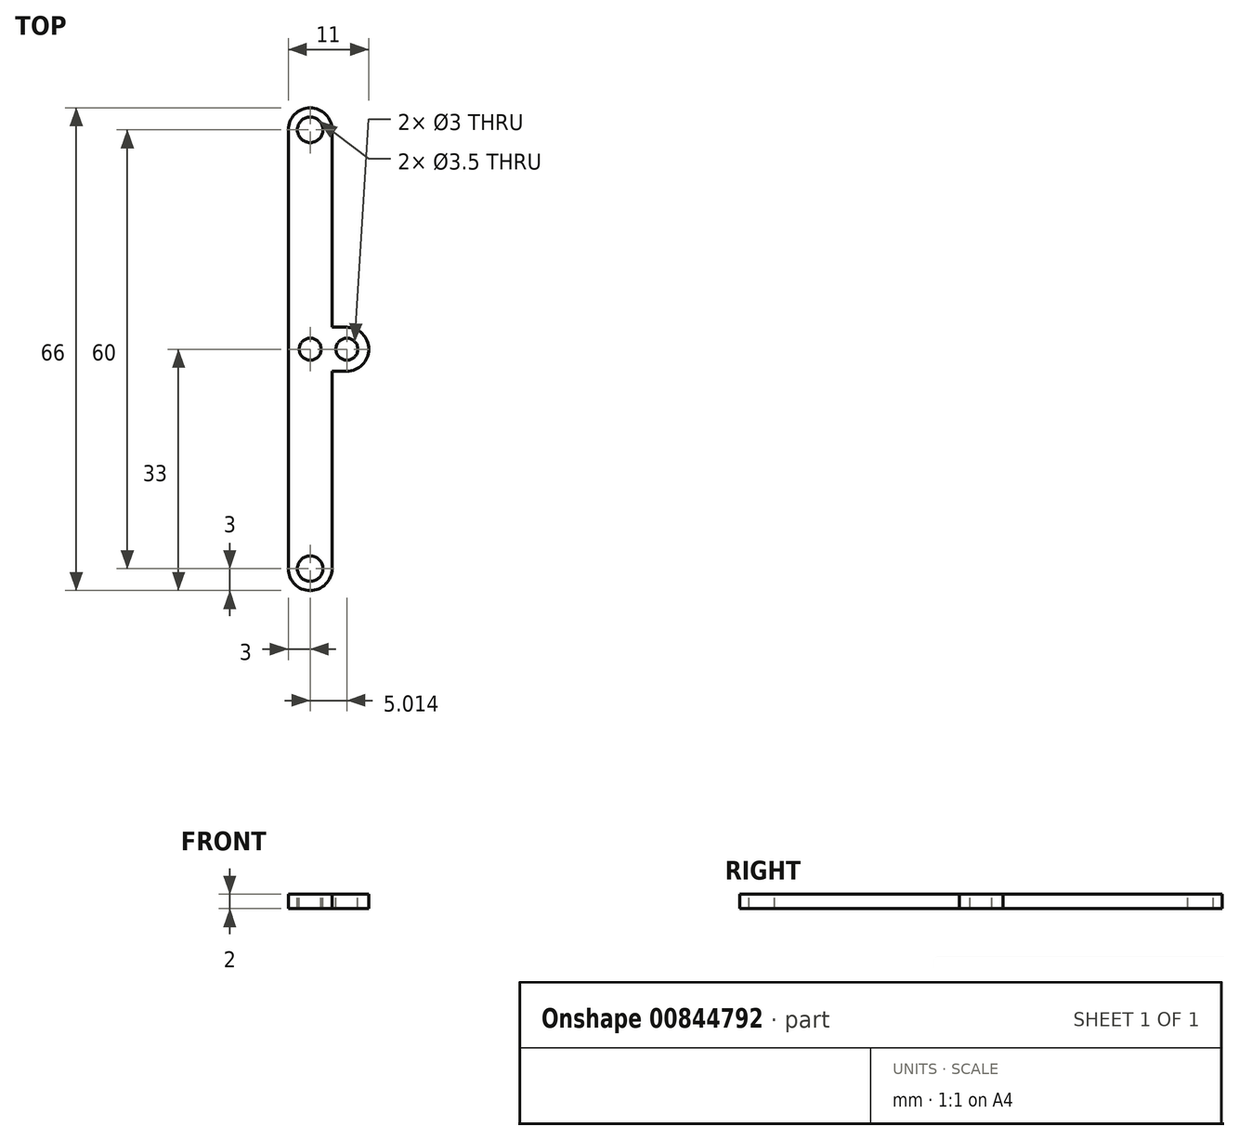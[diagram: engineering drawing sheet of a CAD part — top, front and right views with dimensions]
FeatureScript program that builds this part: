
annotation { "Feature Type Name" : "Feature", "Feature Type Description" : "" }
export const myFeature = defineFeature(function(context is Context, id is Id, definition is map)
    precondition{}
    {
        {
            var Q0;
            Q0=qCreatedBy(makeId("Top.planeOp"),FACE);
            var sketch = newSketch(context, id + "F0", { "sketchPlane" : qUnion([Q0])});
            skLineSegment(sketch, "E0.bottom", {"start": v(-3, 33) * mm, "end": v(3, 33) * mm});
            skLineSegment(sketch, "E0.top", {"start": v(-3, -33) * mm, "end": v(3, -33) * mm});
            skLineSegment(sketch, "E0.left", {"start": v(-3, 33) * mm, "end": v(-3, -33) * mm});
            skLineSegment(sketch, "E0.right", {"start": v(3, 33) * mm, "end": v(3, -33) * mm});
            skPoint(sketch, "E0.middle", {"position": v(0, 0) * mm});
            skSolve(sketch);
        }
        {
            var Q0;
            Q0=qSketchRegion(id+"F0",true);
            extrude(context, id + "F1", {"entities" : qUnion([Q0]), "depth" : 2 * mm, "offsetDistance" : 25 * mm});
        }
        {
            var Q0;
            Q0=makeQuery(id+"F1.opExtrude","CAP_FACE",FACE,{"disambiguationData":[OSD([sQuery(id+"F0.wireOp",EDGE,"E0.bottom"),sQuery(id+"F0.wireOp",EDGE,"E0.top"),sQuery(id+"F0.wireOp",EDGE,"E0.left"),sQuery(id+"F0.wireOp",EDGE,"E0.right")])],"isStart":false});
            var sketch = newSketch(context, id + "F2", { "sketchPlane" : qUnion([Q0])});
            skCircle(sketch, "E1", {"center": v(0, 0) * mm, "radius": 1.5 * mm});
            skLineSegment(sketch, "E2", {"start": v(0, 0) * mm, "end": v(0, 30) * mm});
            skLineSegment(sketch, "E3", {"start": v(0, 0) * mm, "end": v(0, -30) * mm});
            skCircle(sketch, "E4", {"center": v(0, -30) * mm, "radius": 1.75 * mm});
            skCircle(sketch, "E5", {"center": v(0, 30) * mm, "radius": 1.75 * mm});
            skSolve(sketch);
        }
        {
            var Q0;
            Q0=qSketchRegion(id+"F2",true);
            extrude(context, id + "F3", {"entities" : qUnion([Q0]), "operationType" : NewBodyOperationType.REMOVE, "endBound" : BoundingType.UP_TO_NEXT, "oppositeDirection" : true, "depth" : 25 * mm, "offsetDistance" : 25 * mm});
        }
        {
            var Q0;
            Q0=makeQuery(id+"F1.opExtrude","SWEPT_FACE",FACE,{"disambiguationData":[OSD([sQuery(id+"F0.wireOp",EDGE,"E0.right")])]});
            var sketch = newSketch(context, id + "F4", { "sketchPlane" : qUnion([Q0])});
            skLineSegment(sketch, "E6.bottom", {"start": v(0, 2) * mm, "end": v(3, 2) * mm});
            skLineSegment(sketch, "E6.top", {"start": v(0, 0) * mm, "end": v(3, 0) * mm});
            skLineSegment(sketch, "E6.right", {"start": v(3, 2) * mm, "end": v(3, 0) * mm});
            skLineSegment(sketch, "E7", {"start": v(0, 2) * mm, "end": v(-3, 2) * mm});
            skLineSegment(sketch, "E8", {"start": v(-3, 2) * mm, "end": v(-3, 0) * mm});
            skLineSegment(sketch, "E9", {"start": v(-3, 0) * mm, "end": v(0, 0) * mm});
            skSolve(sketch);
        }
        {
            var Q0;
            Q0=qSketchRegion(id+"F4",true);
            extrude(context, id + "F5", {"entities" : qUnion([Q0]), "operationType" : NewBodyOperationType.ADD, "depth" : 5 * mm, "offsetDistance" : 25 * mm});
        }
        {
            var Q0;
            Q0=makeQuery(id+"F5.boolean.opBoolean","MERGE",FACE,{"derivedFrom":[makeQuery(id+"F1.opExtrude","CAP_FACE",FACE,{"disambiguationData":[OSD([sQuery(id+"F0.wireOp",EDGE,"E0.bottom"),sQuery(id+"F0.wireOp",EDGE,"E0.top"),sQuery(id+"F0.wireOp",EDGE,"E0.left"),sQuery(id+"F0.wireOp",EDGE,"E0.right")])],"isStart":false}),makeQuery(id+"F5.opExtrude","SWEPT_FACE",FACE,{"disambiguationData":[OSD([sQuery(id+"F4.wireOp",EDGE,"E6.bottom"),sQuery(id+"F4.wireOp",EDGE,"E7")])]})]});
            var sketch = newSketch(context, id + "F6", { "sketchPlane" : qUnion([Q0])});
            skCircle(sketch, "E10", {"center": v(5.01, 0) * mm, "radius": 1.5 * mm});
            skSolve(sketch);
        }
        {
            var Q0;
            Q0=qSketchRegion(id+"F6",true);
            extrude(context, id + "F7", {"entities" : qUnion([Q0]), "operationType" : NewBodyOperationType.REMOVE, "endBound" : BoundingType.UP_TO_NEXT, "oppositeDirection" : true, "depth" : 25 * mm, "offsetDistance" : 25 * mm});
        }
        {
            var Q0;
            Q0=makeQuery(id+"F1.opExtrude","SWEPT_EDGE",EDGE,{"disambiguationData":[OSD([sQuery(id+"F0.wireOp",EDGE,"E0.top"),sQuery(id+"F0.wireOp",EDGE,"E0.left")])]});
            var Q1;
            Q1=makeQuery(id+"F1.opExtrude","SWEPT_EDGE",EDGE,{"disambiguationData":[OSD([sQuery(id+"F0.wireOp",EDGE,"E0.top"),sQuery(id+"F0.wireOp",EDGE,"E0.right")])]});
            var Q2;
            Q2=makeQuery(id+"F1.opExtrude","SWEPT_EDGE",EDGE,{"disambiguationData":[OSD([sQuery(id+"F0.wireOp",EDGE,"E0.bottom"),sQuery(id+"F0.wireOp",EDGE,"E0.right")])]});
            var Q3;
            Q3=makeQuery(id+"F1.opExtrude","SWEPT_EDGE",EDGE,{"disambiguationData":[OSD([sQuery(id+"F0.wireOp",EDGE,"E0.bottom"),sQuery(id+"F0.wireOp",EDGE,"E0.left")])]});
            var Q4;
            Q4=makeQuery(id+"F5.opExtrude","CAP_EDGE",EDGE,{"disambiguationData":[OSD([sQuery(id+"F4.wireOp",EDGE,"E8")])],"isStart":false});
            var Q5;
            Q5=makeQuery(id+"F5.opExtrude","CAP_EDGE",EDGE,{"disambiguationData":[OSD([sQuery(id+"F4.wireOp",EDGE,"E6.right")])],"isStart":false});
            fillet(context, id + "F8", {"entities" : qUnion([Q0, Q1, Q2, Q3, Q4, Q5]), "radius" : 3 * mm, "tangentPropagation" : true, "allowEdgeOverflow" : false});
        }
    });
